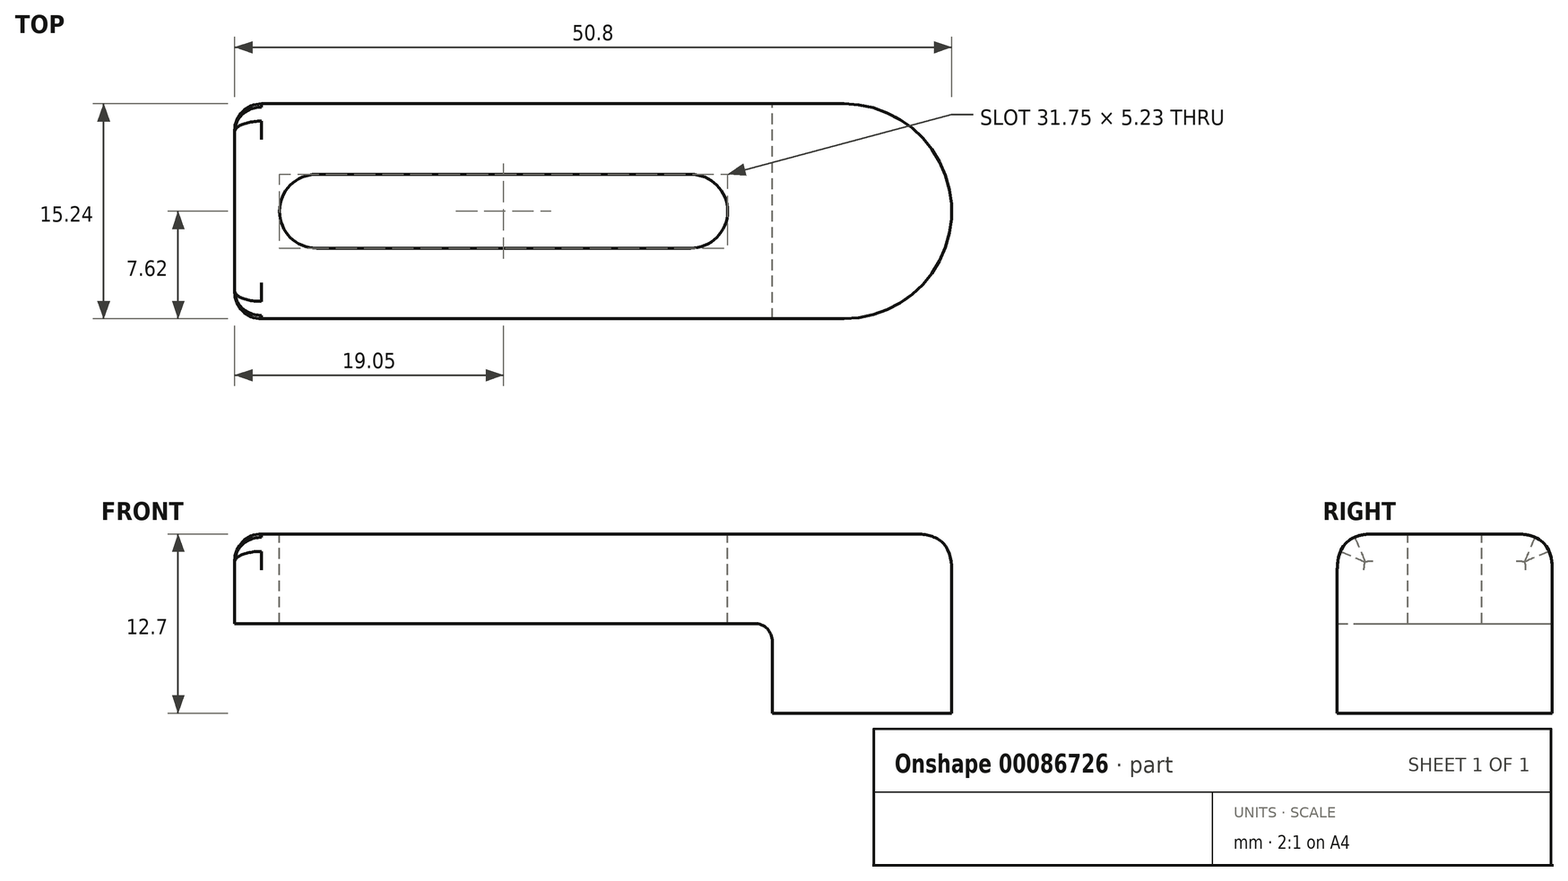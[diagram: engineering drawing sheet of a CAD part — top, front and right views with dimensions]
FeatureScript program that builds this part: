
annotation { "Feature Type Name" : "Feature", "Feature Type Description" : "" }
export const myFeature = defineFeature(function(context is Context, id is Id, definition is map)
    precondition{}
    {
        {
            var Q0;
            Q0=qCreatedBy(makeId("Top.planeOp"),FACE);
            var sketch = newSketch(context, id + "F0", { "sketchPlane" : qUnion([Q0])});
            skLineSegment(sketch, "E0.bottom", {"start": v(17.78, -7.62) * mm, "end": v(-25.4, -7.62) * mm});
            skLineSegment(sketch, "E0.top", {"start": v(17.78, 7.62) * mm, "end": v(-25.4, 7.62) * mm});
            skLineSegment(sketch, "E0.left", {"start": v(25.4, 0) * mm, "end": v(25.4, 0) * mm});
            skLineSegment(sketch, "E0.right", {"start": v(-25.4, -7.62) * mm, "end": v(-25.4, 7.62) * mm});
            skPoint(sketch, "E0.middle", {"position": v(0, 0) * mm});
            skPoint(sketch, "E1.visualSharp", {"position": v(25.4, 7.62) * mm});
            skArc(sketch, "E1.filletArc", {"start": v(25.4, 0) * mm, "mid": v(23.17, 5.39) * mm, "end": v(17.78, 7.62) * mm});
            skPoint(sketch, "E2.visualSharp", {"position": v(25.4, -7.62) * mm});
            skArc(sketch, "E2.filletArc", {"start": v(17.78, -7.62) * mm, "mid": v(23.17, -5.39) * mm, "end": v(25.4, 0) * mm});
            skSolve(sketch);
        }
        {
            var Q0;
            Q0 = qSketchRegion(id + "F0", true);
            extrude(context, id + "F1", {"entities" : qUnion([Q0]), "depth" : 12.7 * mm});
        }
        {
            var Q0;
            Q0=makeQuery(id+"F1.opExtrude","CAP_FACE",FACE,{"disambiguationData":[OSD([sQuery(id+"F0.wireOp",EDGE,"E0.bottom"),sQuery(id+"F0.wireOp",EDGE,"E0.top"),sQuery(id+"F0.wireOp",EDGE,"E0.right"),sQuery(id+"F0.wireOp",EDGE,"E1.filletArc"),sQuery(id+"F0.wireOp",EDGE,"E2.filletArc")])],"isStart":true});
            var sketch = newSketch(context, id + "F2", { "sketchPlane" : qUnion([Q0])});
            skLineSegment(sketch, "E3.bottom", {"start": v(-25.4, 7.62) * mm, "end": v(12.7, 7.62) * mm});
            skLineSegment(sketch, "E3.top", {"start": v(-25.4, -7.62) * mm, "end": v(12.7, -7.62) * mm});
            skLineSegment(sketch, "E3.left", {"start": v(-25.4, 7.62) * mm, "end": v(-25.4, -7.62) * mm});
            skLineSegment(sketch, "E3.right", {"start": v(12.7, 7.62) * mm, "end": v(12.7, -7.62) * mm});
            skSolve(sketch);
        }
        {
            var Q0;
            Q0 = qSketchRegion(id + "F2", true);
            extrude(context, id + "F3", {"entities" : qUnion([Q0]), "operationType" : NewBodyOperationType.REMOVE, "oppositeDirection" : true, "depth" : 6.35 * mm});
        }
        {
            var Q0;
            Q0=makeQuery(id+"F1.opExtrude","CAP_EDGE",EDGE,{"disambiguationData":[OSD([sQuery(id+"F0.wireOp",EDGE,"E0.bottom")])],"isStart":false});
            fillet(context, id + "F4", {"entities" : qUnion([Q0]), "radius" : 2.54 * mm, "tangentPropagation" : true, "rho" : 0.5, "crossSection" : FilletCrossSection.CONIC, "allowEdgeOverflow" : false});
        }
        {
            var Q0;
            Q0=makeQuery(id+"F3.boolean.opBoolean","COPY",EDGE,{"derivedFrom":makeQuery(id+"F3.opExtrude","CAP_EDGE",EDGE,{"disambiguationData":[OSD([sQuery(id+"F2.wireOp",EDGE,"E3.right")])],"isStart":false})});
            var Q1;
            Q1=makeQuery(id+"F3.boolean.opBoolean","COPY",EDGE,{"derivedFrom":makeQuery(id+"F3.opExtrude","CAP_EDGE",EDGE,{"disambiguationData":[OSD([sQuery(id+"F2.wireOp",EDGE,"E3.right")])],"isStart":true})});
            fillet(context, id + "F5", {"entities" : qUnion([Q0, Q1]), "radius" : 1.27 * mm, "tangentPropagation" : true, "allowEdgeOverflow" : false});
        }
        {
            var Q0;
            Q0=makeQuery(id+"F1.opExtrude","CAP_FACE",FACE,{"disambiguationData":[OSD([sQuery(id+"F0.wireOp",EDGE,"E0.bottom"),sQuery(id+"F0.wireOp",EDGE,"E0.top"),sQuery(id+"F0.wireOp",EDGE,"E0.right"),sQuery(id+"F0.wireOp",EDGE,"E1.filletArc"),sQuery(id+"F0.wireOp",EDGE,"E2.filletArc")])],"isStart":false});
            var sketch = newSketch(context, id + "F6", { "sketchPlane" : qUnion([Q0])});
            skLineSegment(sketch, "E4.bottom", {"start": v(6.9, -2.62) * mm, "end": v(-19.6, -2.62) * mm});
            skLineSegment(sketch, "E4.top", {"start": v(6.9, 2.62) * mm, "end": v(-19.6, 2.62) * mm});
            skLineSegment(sketch, "E4.left", {"start": v(9.52, 0) * mm, "end": v(9.52, 0) * mm});
            skLineSegment(sketch, "E4.right", {"start": v(-22.23, 0) * mm, "end": v(-22.23, 0) * mm});
            skPoint(sketch, "E4.middle", {"position": v(-6.35, 0) * mm});
            skPoint(sketch, "E4.middle.positionSnap0", {"position": v(-25.4, 0) * mm});
            skPoint(sketch, "E4.centerSnap0", {"position": v(-25.4, 0) * mm});
            skPoint(sketch, "E5.visualSharp", {"position": v(-22.23, 2.62) * mm});
            skArc(sketch, "E5.filletArc", {"start": v(-19.6, 2.62) * mm, "mid": v(-21.46, 1.85) * mm, "end": v(-22.23, 0) * mm});
            skPoint(sketch, "E6.visualSharp", {"position": v(-22.23, -2.62) * mm});
            skArc(sketch, "E6.filletArc", {"start": v(-22.23, 0) * mm, "mid": v(-21.46, -1.85) * mm, "end": v(-19.6, -2.62) * mm});
            skPoint(sketch, "E7.visualSharp", {"position": v(9.52, -2.62) * mm});
            skArc(sketch, "E7.filletArc", {"start": v(6.9, -2.62) * mm, "mid": v(8.76, -1.85) * mm, "end": v(9.52, 0) * mm});
            skPoint(sketch, "E8.visualSharp", {"position": v(9.52, 2.62) * mm});
            skArc(sketch, "E8.filletArc", {"start": v(9.52, 0) * mm, "mid": v(8.76, 1.85) * mm, "end": v(6.9, 2.62) * mm});
            skSolve(sketch);
        }
        {
            var Q0;
            Q0 = qSketchRegion(id + "F6", true);
            extrude(context, id + "F7", {"entities" : qUnion([Q0]), "operationType" : NewBodyOperationType.REMOVE, "endBound" : BoundingType.UP_TO_NEXT, "oppositeDirection" : true, "depth" : 25.4 * mm});
        }
        {
            var Q0;
            Q0=makeQuery(id+"F1.opExtrude","SWEPT_EDGE",EDGE,{"disambiguationData":[OSD([sQuery(id+"F0.wireOp",EDGE,"E0.top"),sQuery(id+"F0.wireOp",EDGE,"E0.right")])]});
            var Q1;
            Q1=makeQuery(id+"F4.opFillet","BLEND_EDGE",EDGE,{"blendedFrom":[makeQuery(id+"F1.opExtrude","CAP_EDGE",EDGE,{"disambiguationData":[OSD([sQuery(id+"F0.wireOp",EDGE,"E0.top")])],"isStart":false}),makeQuery(id+"F1.opExtrude","SWEPT_FACE",FACE,{"disambiguationData":[OSD([sQuery(id+"F0.wireOp",EDGE,"E0.right")])]})],"blendedInto":[makeQuery(id+"F1.opExtrude","SWEPT_FACE",FACE,{"disambiguationData":[OSD([sQuery(id+"F0.wireOp",EDGE,"E0.right")])]})]});
            fillet(context, id + "F8", {"entities" : qUnion([Q0, Q1]), "radius" : 1.9 * mm, "tangentPropagation" : true, "allowEdgeOverflow" : false});
        }
    });
